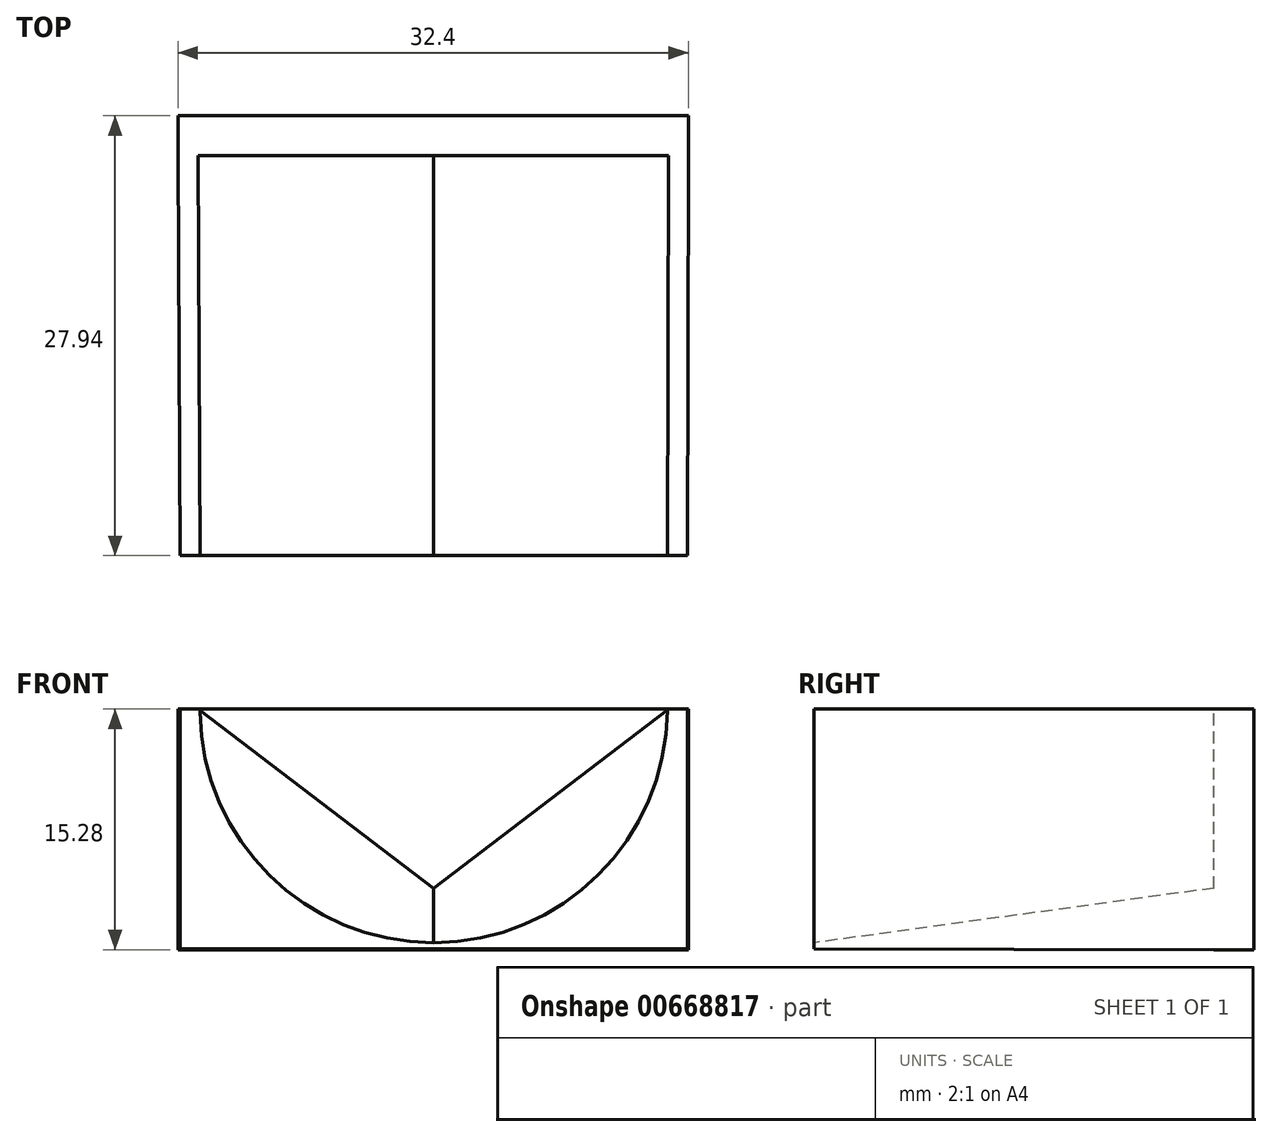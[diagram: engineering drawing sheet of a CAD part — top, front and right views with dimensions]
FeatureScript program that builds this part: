
annotation { "Feature Type Name" : "Feature", "Feature Type Description" : "" }
export const myFeature = defineFeature(function(context is Context, id is Id, definition is map)
    precondition{}
    {
        {
            var Q0;
            Q0=qCreatedBy(makeId("Front.planeOp"),FACE);
            var sketch = newSketch(context, id + "F0", { "sketchPlane" : qUnion([Q0])});
            skCircle(sketch, "E0", {"center": v(0, 0) * mm, "radius": 12.7 * mm, "construction": true});
            skArc(sketch, "E1", {"start": v(-14.84, 0) * mm, "mid": v(0, -14.84) * mm, "end": v(14.84, 0) * mm});
            skLineSegment(sketch, "E2.top", {"start": v(-16.1, -15.24) * mm, "end": v(16.1, -15.24) * mm});
            skLineSegment(sketch, "E2.left", {"start": v(-16.1, 0) * mm, "end": v(-16.1, -15.24) * mm});
            skLineSegment(sketch, "E2.right", {"start": v(16.1, 0) * mm, "end": v(16.1, -15.24) * mm});
            skPoint(sketch, "E3", {"position": v(0, -14.84) * mm});
            skLineSegment(sketch, "E4", {"start": v(-16.1, 0) * mm, "end": v(-14.84, 0) * mm});
            skLineSegment(sketch, "E5", {"start": v(14.84, 0) * mm, "end": v(16.1, 0) * mm});
            skSolve(sketch);
        }
        {
            var Q0;
            Q0=qCreatedBy(makeId("Front.planeOp"),FACE);
            cPlane(context, id + "F1", {"entities" : qUnion([Q0]), "cplaneType" : CPlaneType.OFFSET, "offset" : 25.4 * mm, "oppositeDirection" : true, "width" : 152.4 * mm, "height" : 152.4 * mm});
        }
        {
            var Q0;
            Q0=qCreatedBy(id+"F1.planeOp",FACE);
            var sketch = newSketch(context, id + "F2", { "sketchPlane" : qUnion([Q0])});
            skLineSegment(sketch, "E6.top", {"start": v(-16.23, -15.28) * mm, "end": v(16.17, -15.28) * mm});
            skLineSegment(sketch, "E6.left", {"start": v(-16.23, 0) * mm, "end": v(-16.23, -15.28) * mm});
            skLineSegment(sketch, "E6.right", {"start": v(16.17, 0) * mm, "end": v(16.17, -15.28) * mm});
            skLineSegment(sketch, "E7", {"start": v(-16.23, 0) * mm, "end": v(-14.96, 0) * mm});
            skLineSegment(sketch, "E8", {"start": v(16.17, 0) * mm, "end": v(14.9, 0) * mm});
            skPoint(sketch, "E9", {"position": v(0, -11.37) * mm});
            skLineSegment(sketch, "E10", {"start": v(-14.96, 0) * mm, "end": v(0, -11.37) * mm});
            skLineSegment(sketch, "E11", {"start": v(0, -11.37) * mm, "end": v(14.9, 0) * mm});
            skSolve(sketch);
        }
        {
            var Q0;
            Q0=makeQuery(id+"F2.imprint","IMPRINT",FACE,{"disambiguationData":[TD([[makeQuery(id+"F2.imprint","IMPRINT",EDGE,{"derivedFrom":sQuery(id+"F2.wireOp",EDGE,"E6.top")}),1.0]])]});
            var Q1;
            Q1=makeQuery(id+"F0.imprint","IMPRINT",FACE,{"disambiguationData":[TD([[makeQuery(id+"F0.imprint","IMPRINT",EDGE,{"derivedFrom":sQuery(id+"F0.wireOp",EDGE,"E1")}),-1.0]])]});
            var Q2;
            Q2=sQuery(id+"F2.wireOp",VERTEX,"E9");
            var Q3;
            Q3=sQuery(id+"F0.wireOp",VERTEX,"E3");
            loft(context, id + "F3", {"sheetProfilesArray" : [{ "sheetProfileEntities" : qUnion([Q0]) }, { "sheetProfileEntities" : qUnion([Q1]) }], "matchConnections" : true, "connections" : [{ "connectionEntities" : qUnion([Q2, Q3]), "connectionEdgeQueries" : qUnion([]), "connectionEdgeParameters" : [] }]});
        }
        {
            var Q0;
            Q0=makeQuery(id+"F3.opLoft","CAP_FACE",FACE,{"disambiguationData":[OSD([makeQuery(id+"F2.imprint","IMPRINT",FACE,{"disambiguationData":[TD([[makeQuery(id+"F2.imprint","IMPRINT",EDGE,{"derivedFrom":sQuery(id+"F2.wireOp",EDGE,"E6.top")}),1.0]])]})])],"isStart":true});
            var sketch = newSketch(context, id + "F4", { "sketchPlane" : qUnion([Q0])});
            skLineSegment(sketch, "E12.bottom", {"start": v(-16.17, 0) * mm, "end": v(16.23, 0) * mm});
            skLineSegment(sketch, "E12.top", {"start": v(-16.17, -15.28) * mm, "end": v(16.23, -15.28) * mm});
            skLineSegment(sketch, "E12.left", {"start": v(-16.17, 0) * mm, "end": v(-16.17, -15.28) * mm});
            skLineSegment(sketch, "E12.right", {"start": v(16.23, 0) * mm, "end": v(16.23, -15.28) * mm});
            skSolve(sketch);
        }
        {
            var Q0;
            Q0 = qSketchRegion(id + "F4", true);
            extrude(context, id + "F5", {"entities" : qUnion([Q0]), "operationType" : NewBodyOperationType.ADD, "depth" : 2.54 * mm, "offsetDistance" : 25.4 * mm});
        }
    });
